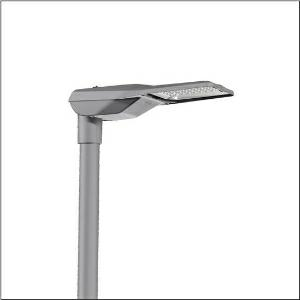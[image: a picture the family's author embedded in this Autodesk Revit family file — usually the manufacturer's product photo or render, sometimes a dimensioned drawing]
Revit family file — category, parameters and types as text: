
# Revit family: streetlight_sl_21_mini___st1_5a_5xe2p33s08gb_ee16
name_source: partatom
category: Lighting Fixtures
units: mm (PartAtom-declared; Revit-internal decimal feet)

## family parameters
Cut with Voids When Loaded = No
Host = Face
Light Source = No
Part Type = Normal
Room Calculation Point = No
Round Connector Dimension = Use Diameter
Shared = No

## types (1)
- --- (1 x LED, 5840 lm, 40.4 W, 3000K)
    Apparent Load = 40 VA
    CIE Flux Codes = 22 53 95 100 100
    Color Rendering = 70
    Color Temperature = 3000K
    Default Elevation = 1800 mm
    Description = Streetlight SL 21 mini, mast luminaire, primary light control with lens, of PMMA, primary optical cover: cover, of toughened safety glass, transparent, light distribution: ST1.5a, light emission: direct distribution, primary light characteristic: asymmetric, installation type: side-entry, post-top, LED, High Power LED, rated luminous flux: 5.840lm, luminous efficacy: 145lm/W, light colour: 730, colour temperature: 3000K, control gear: D4i, control: overheat protection, constant luminous flux control, time-dependent luminous flux control, flexible luminous flux parameterisation, pre-setting: logarithmic dimming characteristic, mains connection: 220..240V, AC, 50/60Hz, start of lifetime: 40W, end of service life: 41W, reduction: 19W, luminaire housing, of diecast aluminium, powder-coated, Siteco® metallic grey (DB 702S), corrosivity category C5 mid according to DIN EN ISO 12944, please order mast flange separately, inclination adjustable: 0°, 5°, 10°, 15°, sealing non-destructively replaceable, multi-level sealing system, length: 628mm, width: 235mm, height: 110mm, mast flange for spigot size: 42mm (side-entry): 5XC10008XM4, 60/48mm (side-entry/post-top): 5XC10108XM2, 76/60mm (side-entry/post-top): 5XC10108XM1, mounting height: 4..8m, Smart Interface above, protection rating (complete): IP66, insulation class (complete): insulation class II (safety insulation), certification: CE, ENEC, ENEC+, VDE, impact resistance: IK10, permissible operating ambient temperature for outdoor applications: -40..+50°C, standard-compliant lighting for roads and squares, packaging unit: 1 piece

Light Distribution: ST1.5a
    Height = 110 mm
    Lamp = 1 x LED
    Lamp Light Flux = 5840 lm
    Lamp Power = 40.4 W
    Lamp count = 1
    Length = 625 mm
    Luminous efficacy = 145 lm/W
    Manufacturer = Siteco
    ModVariant = No
    Model = 5XE2P33S08GB
    Number of Poles = 1
    OnlyDefault = Yes
    Power Factor = 1
    Product Name = Streetlight SL 21 mini | ST1.5a
    Product group = mast luminaire | pylon top
    ProductGroupID = 6100
    Protection Class = Protection class II
    Protection Degree = IP 66
    RLX_Detail_Level = 1
    RLX_Emergency_Light_Flux = 0 lm
    RLX_Emergency_Type = 0
    RLX_Emergency_Type_DB = No
    RlxData = <blob elided: 29741 chars, md5=16b4ea69>
    Socket = socket
    Standby Power = 0 W
    System Light Flux = 5840 lm
    System Power = 40 W
    Type Comments = factory setting: luminous flux: 100 % | dim-lin: 254 | 812 mA
    Type Image = l_1003515.jpg
    URL = http://relux.com
    VarID = @adj_175714
    Voltage = 0 V
    Weight = 0.00 kg
    Width = 234 mm

## geometry (parser evidence)
native form markers: Blend x4, Sweep x8
no freeform markers — native parametric forms only
